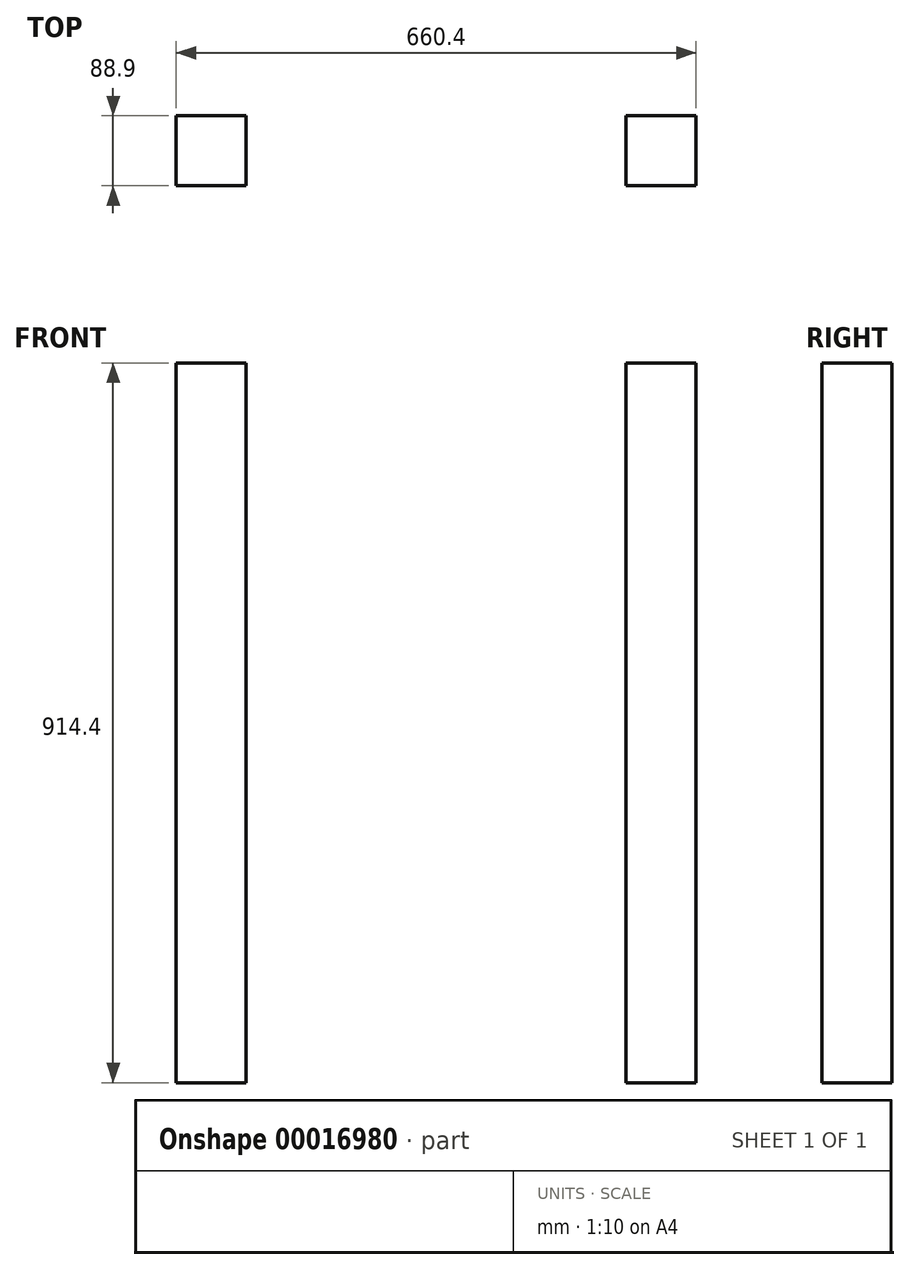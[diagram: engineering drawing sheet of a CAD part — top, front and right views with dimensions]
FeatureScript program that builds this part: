
annotation { "Feature Type Name" : "Feature", "Feature Type Description" : "" }
export const myFeature = defineFeature(function(context is Context, id is Id, definition is map)
    precondition{}
    {
        {
            var Q0;
            Q0=qCreatedBy(makeId("Top.planeOp"),FACE);
            var sketch = newSketch(context, id + "F0", { "sketchPlane" : qUnion([Q0])});
            skLineSegment(sketch, "E0.rect.bottom", {"start": v(-44.45, -44.45) * mm, "end": v(44.45, -44.45) * mm});
            skLineSegment(sketch, "E0.rect.top", {"start": v(-44.45, 44.45) * mm, "end": v(44.45, 44.45) * mm});
            skLineSegment(sketch, "E0.rect.left", {"start": v(-44.45, -44.45) * mm, "end": v(-44.45, 44.45) * mm});
            skLineSegment(sketch, "E0.rect.right", {"start": v(44.45, -44.45) * mm, "end": v(44.45, 44.45) * mm});
            skPoint(sketch, "E0.rect.middle", {"position": v(0, 0) * mm});
            skLineSegment(sketch, "E1", {"start": v(285.75, -15.74) * mm, "end": v(285.75, -34.85) * mm, "construction": true});
            skLineSegment(sketch, "E2.MirrorCS", {"start": v(615.95, 44.45) * mm, "end": v(527.05, 44.45) * mm});
            skLineSegment(sketch, "E3.MirrorCS", {"start": v(615.95, -44.45) * mm, "end": v(615.95, 44.45) * mm});
            skLineSegment(sketch, "E4.MirrorCS", {"start": v(527.05, -44.45) * mm, "end": v(527.05, 44.45) * mm});
            skLineSegment(sketch, "E5.MirrorCS", {"start": v(615.95, -44.45) * mm, "end": v(527.05, -44.45) * mm});
            skLineSegment(sketch, "E6.bottom", {"start": v(590.55, -82.55) * mm, "end": v(-19.05, -82.55) * mm});
            skLineSegment(sketch, "E6.top", {"start": v(590.55, -44.45) * mm, "end": v(-19.05, -44.45) * mm});
            skLineSegment(sketch, "E6.left", {"start": v(590.55, -82.55) * mm, "end": v(590.55, -44.45) * mm});
            skLineSegment(sketch, "E6.right", {"start": v(-19.05, -82.55) * mm, "end": v(-19.05, -44.45) * mm});
            skSolve(sketch);
        }
        {
            var Q0;
            {var subQ2=sQuery(id+"F0.wireOp",EDGE,"E0.rect.bottom");Q0=makeQuery(id+"F0.imprint","IMPRINT",FACE,{"disambiguationData":[TD([[makeQuery(id+"F0.imprint","IMPRINT",EDGE,{"derivedFrom":subQ2}),1.0]])]});}
            var Q1;
            Q1=makeQuery(id+"F0.imprint","IMPRINT",FACE,{"disambiguationData":[TD([[makeQuery(id+"F0.imprint","IMPRINT",EDGE,{"derivedFrom":sQuery(id+"F0.wireOp",EDGE,"E2.MirrorCS")}),1.0]])]});
            extrude(context, id + "F1", {"entities" : qUnion([Q0, Q1]), "depth" : 914.4 * mm});
        }
    });
